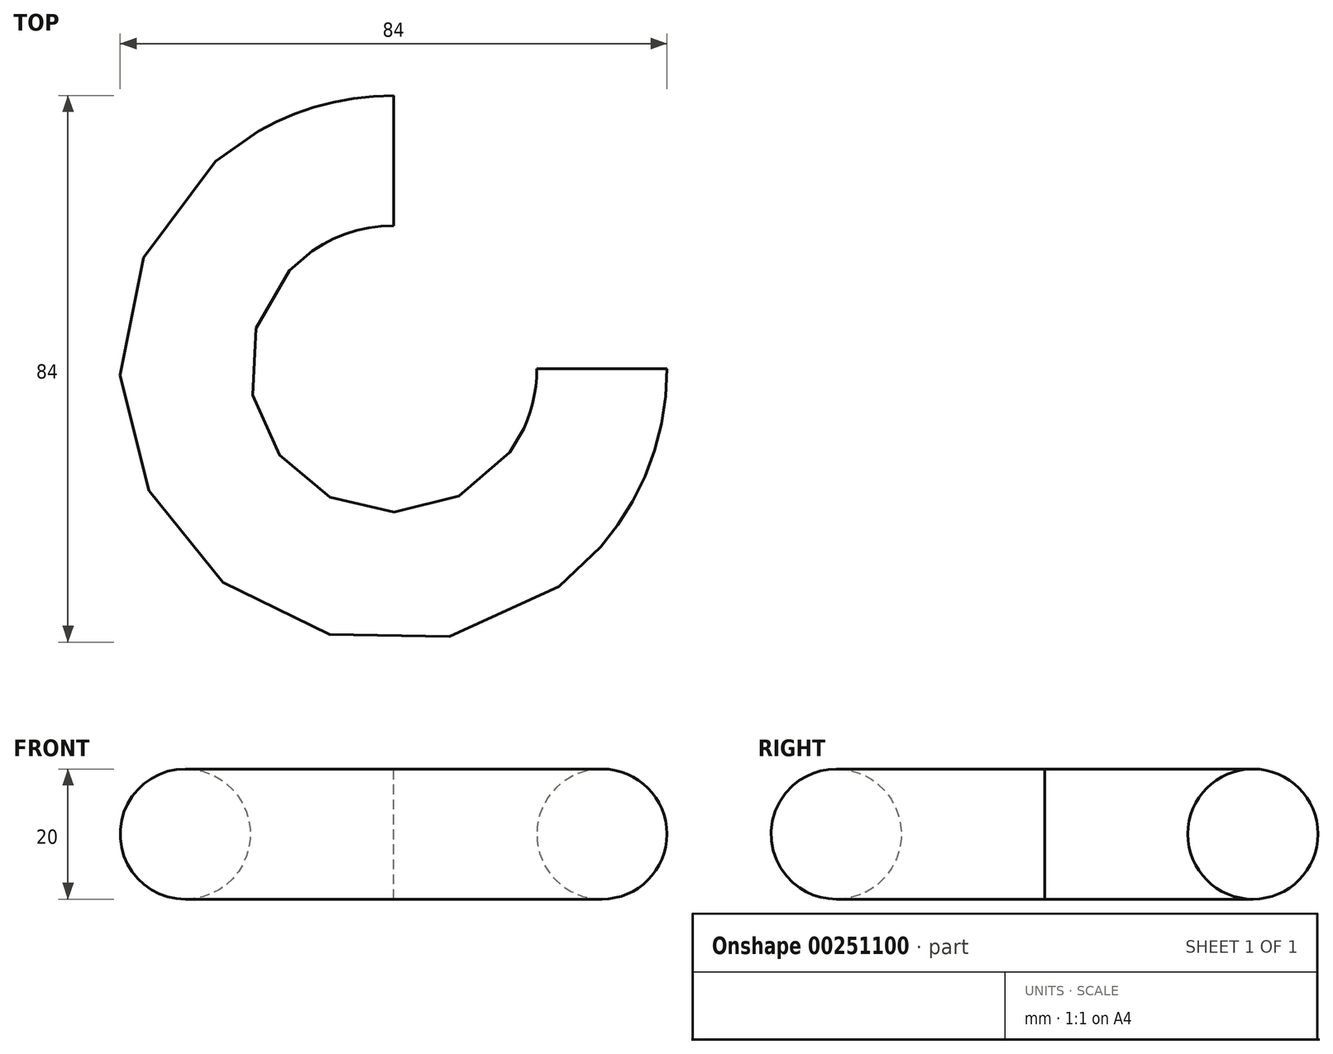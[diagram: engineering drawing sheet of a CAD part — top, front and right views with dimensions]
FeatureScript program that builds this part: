
annotation { "Feature Type Name" : "Feature", "Feature Type Description" : "" }
export const myFeature = defineFeature(function(context is Context, id is Id, definition is map)
    precondition{}
    {
        {
            var Q0;
            Q0=qCreatedBy(makeId("Front.planeOp"),FACE);
            var sketch = newSketch(context, id + "F0", { "sketchPlane" : qUnion([Q0]), "disableImprinting" : false});
            skCircle(sketch, "E0", {"center": v(32, 0) * mm, "radius": 10 * mm});
            skLineSegment(sketch, "E1", {"start": v(0, 29.01) * mm, "end": v(0, -56.84) * mm, "construction": true});
            skSolve(sketch);
        }
        {
            var Q0;
            Q0=makeQuery(id+"F0.imprint","IMPRINT",FACE,{"disambiguationData":[TD([[makeQuery(id+"F0.imprint","IMPRINT",EDGE,{"derivedFrom":sQuery(id+"F0.wireOp",EDGE,"E0")}),1.0]])]});
            var Q1;
            Q1=sQuery(id+"F0.wireOp",EDGE,"E1");
            var Q2;
            Q2=sQuery(id+"F0.wireOp",EDGE,"E1");
            revolve(context, id + "F1", {"entities" : qUnion([Q0]), "surfaceEntities" : qUnion([Q1]), "axis" : qUnion([Q2]), "revolveType" : RevolveType.ONE_DIRECTION, "angle" : 270 * degree});
        }
    });
